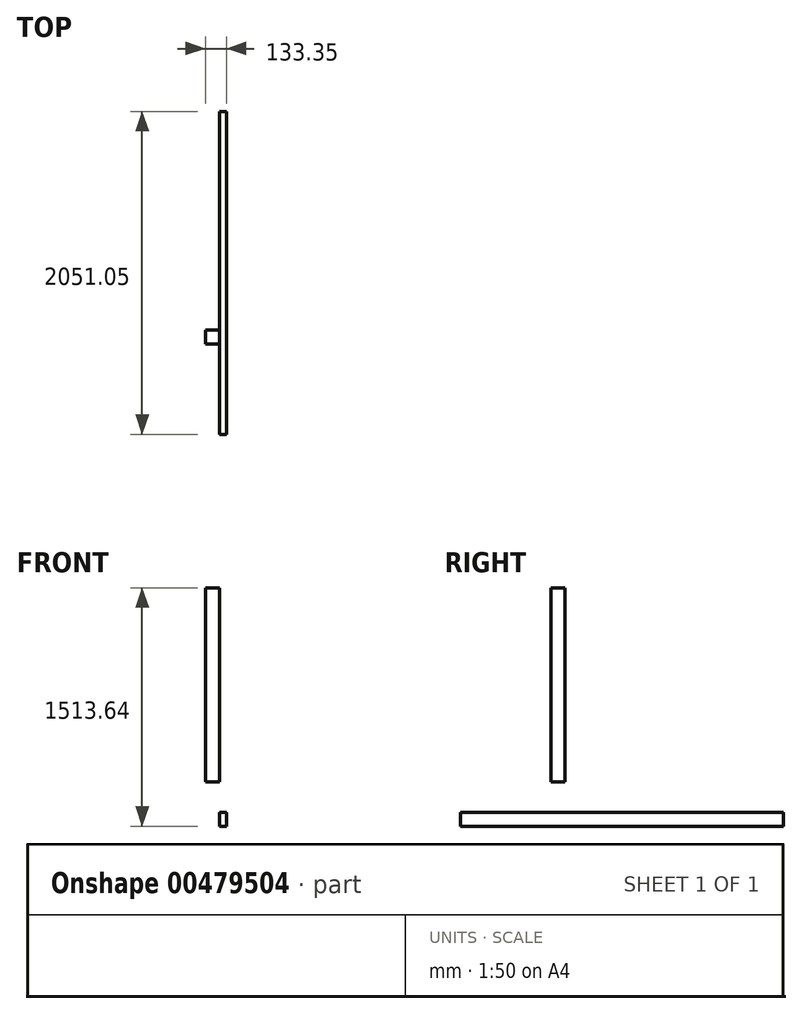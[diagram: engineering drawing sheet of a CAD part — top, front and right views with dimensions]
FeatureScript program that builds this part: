
annotation { "Feature Type Name" : "Feature", "Feature Type Description" : "" }
export const myFeature = defineFeature(function(context is Context, id is Id, definition is map)
    precondition{}
    {
        {
            var Q0;
            Q0=qCreatedBy(makeId("Top.planeOp"),FACE);
            var sketch = newSketch(context, id + "F0", { "sketchPlane" : qUnion([Q0])});
            skLineSegment(sketch, "E0.bottom", {"start": v(0, 0) * mm, "end": v(-88.9, 0) * mm});
            skLineSegment(sketch, "E0.top", {"start": v(0, 88.9) * mm, "end": v(-88.9, 88.9) * mm});
            skLineSegment(sketch, "E0.left", {"start": v(0, 0) * mm, "end": v(0, 88.9) * mm});
            skLineSegment(sketch, "E0.right", {"start": v(-88.9, 0) * mm, "end": v(-88.9, 88.9) * mm});
            skSolve(sketch);
        }
        {
            var Q0;
            Q0=makeQuery(id+"F0.imprint","IMPRINT",FACE,{"disambiguationData":[TD([[makeQuery(id+"F0.imprint","IMPRINT",EDGE,{"derivedFrom":sQuery(id+"F0.wireOp",EDGE,"E0.bottom")}),-1.0]])]});
            extrude(context, id + "F1", {"entities" : qUnion([Q0]), "depth" : 1231.9 * mm});
        }
        {
            var Q0;
            Q0=qCreatedBy(makeId("Right.planeOp"),FACE);
            var sketch = newSketch(context, id + "F2", { "sketchPlane" : qUnion([Q0])});
            skLineSegment(sketch, "E1.bottom", {"start": v(1477.1, -192.84) * mm, "end": v(-573.95, -192.84) * mm});
            skLineSegment(sketch, "E1.top", {"start": v(1477.1, -281.74) * mm, "end": v(-573.95, -281.74) * mm});
            skLineSegment(sketch, "E1.left", {"start": v(1477.1, -192.84) * mm, "end": v(1477.1, -281.74) * mm});
            skLineSegment(sketch, "E1.right", {"start": v(-573.95, -192.84) * mm, "end": v(-573.95, -281.74) * mm});
            skSolve(sketch);
        }
        {
            var Q0;
            Q0=makeQuery(id+"F2.imprint","IMPRINT",FACE,{"disambiguationData":[TD([[makeQuery(id+"F2.imprint","IMPRINT",EDGE,{"derivedFrom":sQuery(id+"F2.wireOp",EDGE,"E1.bottom")}),1.0]])]});
            extrude(context, id + "F3", {"entities" : qUnion([Q0]), "depth" : 44.45 * mm});
        }
    });
